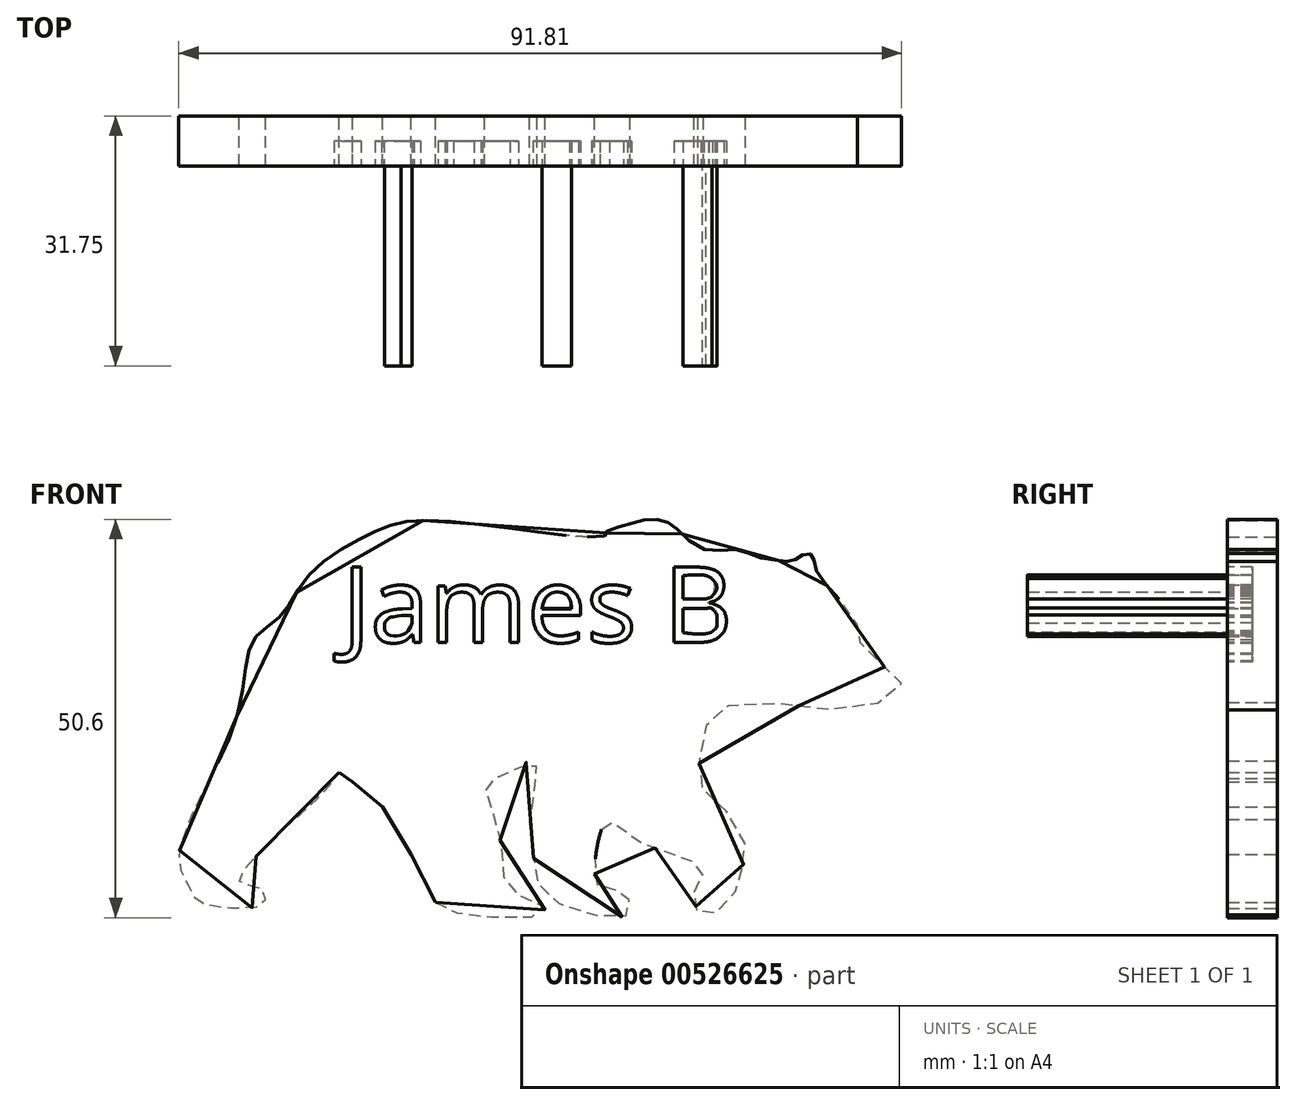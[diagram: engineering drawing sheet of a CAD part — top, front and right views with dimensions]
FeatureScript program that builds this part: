
annotation { "Feature Type Name" : "Feature", "Feature Type Description" : "" }
export const myFeature = defineFeature(function(context is Context, id is Id, definition is map)
    precondition{}
    {
        {
            var Q0;
            Q0=qCreatedBy(makeId("Front.planeOp"),FACE);
            var sketch = newSketch(context, id + "F0", { "sketchPlane" : qUnion([Q0])});
            skLineSegment(sketch, "E0", {"start": v(-22.8, 11.9) * mm, "end": v(-21.08, 10.75) * mm});
            skLineSegment(sketch, "E1", {"start": v(-21.08, 10.75) * mm, "end": v(-17.32, 7.58) * mm});
            skLineSegment(sketch, "E2", {"start": v(-17.32, 7.58) * mm, "end": v(-13.67, 1.51) * mm});
            skLineSegment(sketch, "E3", {"start": v(-13.67, 1.51) * mm, "end": v(-10.59, -4.55) * mm});
            skPoint(sketch, "E4.69.internal.snap0", {"position": v(-19.2, 9.16) * mm});
            skPoint(sketch, "E4.87.internal.snap0", {"position": v(-19.2, 9.16) * mm});
            skFitSpline(sketch, "E4", {"points": [v(-10.59, -4.55) * mm, v(-8.16, -5.82) * mm, v(-2.34, -6.46) * mm, v(3.16, -5.98) * mm, v(3.03, -5.02) * mm, v(0, -3.69) * mm, v(-1.74, -1.92) * mm, v(-2.18, 2.8) * mm, v(-2.28, 2.98) * mm, v(-3.2, 6.92) * mm, v(-4.2, 11.04) * mm, v(-1.6, 11.32) * mm, v(1.25, 13.36) * mm, v(2.2, 12.81) * mm, v(2.07, 10.36) * mm, v(1.39, 4.78) * mm, v(2.07, 0) * mm, v(2.75, -2.84) * mm, v(7.51, -5.7) * mm, v(13.23, -6.37) * mm, v(14.11, -5.73) * mm, v(13.97, -4.1) * mm, v(13.4, -3.38) * mm, v(11.15, -2.8) * mm, v(9.93, -2.22) * mm, v(9.79, 1.35) * mm, v(10.97, 5.58) * mm, v(11.64, 5.91) * mm, v(12.84, 4.47) * mm, v(22.37, 0.52) * mm, v(23.48, -0.44) * mm, v(22.85, -1.98) * mm, v(22.27, -3.23) * mm, v(22.47, -4.55) * mm, v(22.75, -5.92) * mm, v(24.77, -5.97) * mm, v(27.32, -3.76) * mm, v(28.2, -0.73) * mm, v(28.48, 0) * mm, v(28.53, 3.99) * mm, v(24.78, 8.4) * mm, v(22.83, 11.14) * mm, v(23.64, 16.4) * mm, v(24.8, 19.65) * mm, v(32.7, 20.74) * mm, v(43.85, 20.2) * mm, v(48.61, 23.05) * mm, v(47.8, 24.16) * mm, v(44.32, 27.4) * mm, v(42.95, 29.26) * mm, v(43.03, 30.72) * mm, v(40.3, 34.4) * mm, v(37.64, 37.96) * mm, v(37.37, 39.46) * mm, v(36.7, 39.73) * mm, v(35.67, 39.39) * mm, v(34.85, 38.84) * mm, v(33.09, 38.84) * mm, v(30.1, 39.39) * mm, v(27.5, 40.27) * mm, v(23.7, 40.2) * mm, v(20.02, 42.93) * mm, v(18.48, 43.89) * mm, v(16.03, 44.03) * mm, v(13.82, 43.4) * mm, v(11.27, 42.59) * mm, v(11.12, 42.1) * mm, v(2.22, 42.5) * mm, v(-13.4, 43.92) * mm, v(-19.2, 42.08) * mm, v(-26.5, 37.18) * mm, v(-30.23, 31.84) * mm, v(-33.79, 28.6) * mm, v(-35.57, 19.87) * mm, v(-40.99, 7.7) * mm, v(-42.36, 4.38) * mm, v(-43.06, 2.2) * mm, v(-42.92, -0.52) * mm, v(-41.43, -3.44) * mm, v(-40.61, -4.55) * mm, v(-33, -5.07) * mm, v(-32.17, -3.92) * mm, v(-33, -2.62) * mm, v(-35.1, -2.28) * mm, v(-35.44, -1.33) * mm, v(-32.51, 2.07) * mm, v(-29.11, 5.4) * mm, v(-25.03, 9.16) * mm, v(-22.8, 11.9) * mm], "startDerivative": vector(206.86, -137.7) * mm, "endDerivative": vector(164.22, 225.3) * mm});
            skSolve(sketch);
        }
        {
            var Q0;
            Q0 = qSketchRegion(id + "F0", true);
            extrude(context, id + "F1", {"entities" : qUnion([Q0]), "depth" : 6.35 * mm, "offsetDistance" : 25.4 * mm});
        }
        {
            var Q0;
            Q0=makeQuery(id+"F1.opExtrude","CAP_FACE",FACE,{"disambiguationData":[OSD([sQuery(id+"F0.wireOp",EDGE,"E0"),sQuery(id+"F0.wireOp",EDGE,"E1"),sQuery(id+"F0.wireOp",EDGE,"E2"),sQuery(id+"F0.wireOp",EDGE,"E3"),sQuery(id+"F0.wireOp",EDGE,"E4")])],"isStart":false});
            var sketch = newSketch(context, id + "F2", { "sketchPlane" : qUnion([Q0])});
            skText(sketch, "E5", { "text": "James B", "fontName": "OpenSans-Regular.ttf"});
            const initialGuessF2  = {"E5": [-0.02241, 0.02846, 1, 0, 0.00964]};
            skSetInitialGuess(sketch, initialGuessF2);
            skSolve(sketch);
        }
        {
            var Q0;
            Q0=makeQuery(id+"F2.imprint","IMPRINT",FACE,{"disambiguationData":[TD([[makeQuery(id+"F2.imprint","IMPRINT",EDGE,{"derivedFrom":sQuery(id+"F2.wireOp",EDGE,"E5.sketch_text.stroke-0")}),1.0]])]});
            var sketch = newSketch(context, id + "F3", { "sketchPlane" : qUnion([Q0])});
            skLineSegment(sketch, "E6", {"start": v(-21.16, 38.02) * mm, "end": v(-21.16, 28.58) * mm});
            skLineSegment(sketch, "E7", {"start": v(-21.16, 38.02) * mm, "end": v(-19.95, 38.02) * mm});
            skLineSegment(sketch, "E8", {"start": v(-19.95, 38.02) * mm, "end": v(-19.95, 28.64) * mm});
            skFitSpline(sketch, "E9", {"points": [v(-21.16, 28.58) * mm, v(-21.16, 27.92) * mm, v(-21.82, 27.2) * mm, v(-23.27, 27) * mm, v(-23.4, 26.16) * mm, v(-22.6, 26.04) * mm, v(-21.7, 26.1) * mm, v(-20.73, 26.59) * mm, v(-19.95, 27.67) * mm], "startDerivative": vector(0.93, -6.27) * mm, "endDerivative": vector(4.85, 8.31) * mm});
            skLineSegment(sketch, "E10", {"start": v(-19.95, 28.64) * mm, "end": v(-19.95, 27.67) * mm});
            skLineSegment(sketch, "E11", {"start": v(-17.3, 35.15) * mm, "end": v(-17, 34.47) * mm});
            skLineSegment(sketch, "E12", {"start": v(-13.47, 29.43) * mm, "end": v(-13.22, 28.52) * mm});
            skLineSegment(sketch, "E13", {"start": v(-13.56, 31.9) * mm, "end": v(-13.56, 30.9) * mm});
            skLineSegment(sketch, "E14", {"start": v(-13.22, 28.52) * mm, "end": v(-12.53, 28.52) * mm});
            skLineSegment(sketch, "E15", {"start": v(-12.53, 28.52) * mm, "end": v(-12.53, 33.42) * mm});
            skLineSegment(sketch, "E16", {"start": v(-13.56, 32.84) * mm, "end": v(-13.56, 33.48) * mm});
            skFitSpline(sketch, "E17", {"points": [v(-17.3, 35.15) * mm, v(-16.1, 35.63) * mm, v(-14.92, 35.72) * mm, v(-14.04, 35.63) * mm, v(-13.13, 35.15) * mm, v(-12.53, 34.24) * mm, v(-12.53, 33.42) * mm], "startDerivative": vector(6.35, 3.06) * mm, "endDerivative": vector(-0.75, -5.45) * mm});
            skFitSpline(sketch, "E18", {"points": [v(-17, 34.47) * mm, v(-16.18, 34.78) * mm, v(-15.27, 34.96) * mm, v(-14.46, 34.9) * mm, v(-13.7, 34.47) * mm, v(-13.56, 33.48) * mm], "startDerivative": vector(4.02, 1.7) * mm, "endDerivative": vector(-0.15, -5.26) * mm});
            skFitSpline(sketch, "E19", {"points": [v(-13.56, 32.84) * mm, v(-14.6, 32.84) * mm, v(-16.42, 32.57) * mm, v(-17.88, 31.82) * mm, v(-18.27, 30.27) * mm, v(-17.97, 29.33) * mm, v(-17.33, 28.64) * mm, v(-16.21, 28.34) * mm, v(-14.43, 28.55) * mm, v(-13.47, 29.43) * mm], "startDerivative": vector(-9.94, 0.36) * mm, "endDerivative": vector(7.38, 9.37) * mm});
            skFitSpline(sketch, "E20", {"points": [v(-13.56, 31.9) * mm, v(-14.97, 31.9) * mm], "startDerivative": vector(-1.42, 0) * mm, "endDerivative": vector(-1.42, 0) * mm});
            skFitSpline(sketch, "E21", {"points": [v(-14.97, 31.9) * mm, v(-15.85, 31.72) * mm, v(-16.33, 31.63) * mm, v(-17, 30.97) * mm, v(-17.03, 30.33) * mm, v(-16.88, 29.73) * mm, v(-16.21, 29.3) * mm, v(-14.97, 29.33) * mm, v(-14, 29.94) * mm, v(-13.56, 30.9) * mm], "startDerivative": vector(-8.4, -2.05) * mm, "endDerivative": vector(2.73, 8.36) * mm});
            skLineSegment(sketch, "E22", {"start": v(-10.25, 35.6) * mm, "end": v(-10.25, 28.58) * mm});
            skLineSegment(sketch, "E23", {"start": v(-5.65, 33.33) * mm, "end": v(-5.65, 28.62) * mm});
            skLineSegment(sketch, "E24", {"start": v(-4.49, 33.35) * mm, "end": v(-4.49, 28.57) * mm});
            skLineSegment(sketch, "E25", {"start": v(-9.07, 33.2) * mm, "end": v(-9.07, 28.62) * mm});
            skLineSegment(sketch, "E26", {"start": v(-9.3, 35.6) * mm, "end": v(-9.3, 34.79) * mm});
            skLineSegment(sketch, "E27", {"start": v(-5.65, 28.62) * mm, "end": v(-4.49, 28.57) * mm});
            skLineSegment(sketch, "E28", {"start": v(0, 33.46) * mm, "end": v(0, 28.59) * mm});
            skLineSegment(sketch, "E29", {"start": v(0, 28.59) * mm, "end": v(-1.09, 28.59) * mm});
            skLineSegment(sketch, "E30", {"start": v(-1.09, 28.59) * mm, "end": v(-1.09, 33.42) * mm});
            skFitSpline(sketch, "E31", {"points": [v(-9.07, 33.2) * mm, v(-8.7, 34.2) * mm, v(-7.98, 34.66) * mm, v(-6.95, 34.88) * mm, v(-6.05, 34.58) * mm, v(-5.65, 33.33) * mm], "startDerivative": vector(1.27, 5.5) * mm, "endDerivative": vector(1, -6.51) * mm});
            skLineSegment(sketch, "E32", {"start": v(-10.25, 35.6) * mm, "end": v(-9.3, 35.6) * mm});
            skFitSpline(sketch, "E33", {"points": [v(-4.49, 33.35) * mm, v(-4.3, 33.98) * mm, v(-4.06, 34.28) * mm, v(-3.83, 34.52) * mm, v(-3.44, 34.72) * mm, v(-3.05, 34.8) * mm, v(-2.75, 34.83) * mm, v(-2.5, 34.83) * mm, v(-2.16, 34.8) * mm, v(-1.79, 34.67) * mm, v(-1.42, 34.37) * mm], "startDerivative": vector(1.09, 5.4) * mm, "endDerivative": vector(3.24, -3.12) * mm});
            skFitSpline(sketch, "E34", {"points": [v(-1.09, 33.42) * mm, v(-1.17, 33.77) * mm, v(-1.27, 34.1) * mm, v(-1.42, 34.37) * mm], "startDerivative": vector(-0.21, 1.02) * mm, "endDerivative": vector(-0.49, 0.8) * mm});
            skLineSegment(sketch, "E35", {"start": v(-10.25, 28.58) * mm, "end": v(-9.07, 28.62) * mm});
            skFitSpline(sketch, "E36", {"points": [v(0, 33.46) * mm, v(-0.15, 34.31) * mm, v(-0.6, 35.11) * mm, v(-1.35, 35.6) * mm, v(-2.01, 35.74) * mm, v(-2.88, 35.74) * mm, v(-3.5, 35.58) * mm, v(-4.24, 35.17) * mm, v(-4.68, 34.66) * mm, v(-4.74, 34.56) * mm, v(-4.8, 34.55) * mm, v(-4.95, 34.85) * mm], "startDerivative": vector(-0.88, 7.61) * mm, "endDerivative": vector(-2.24, 5.77) * mm});
            skFitSpline(sketch, "E37", {"points": [v(-4.95, 34.85) * mm, v(-5.33, 35.26) * mm, v(-6.08, 35.65) * mm], "startDerivative": vector(-0.71, 0.97) * mm, "endDerivative": vector(-1.5, 0.66) * mm});
            skFitSpline(sketch, "E38", {"points": [v(-6.08, 35.65) * mm, v(-6.75, 35.78) * mm, v(-7.65, 35.7) * mm, v(-8.64, 35.25) * mm, v(-9.01, 34.85) * mm, v(-9.1, 34.63) * mm, v(-9.17, 34.62) * mm, v(-9.3, 34.79) * mm], "startDerivative": vector(-3.77, 0.94) * mm, "endDerivative": vector(-1.28, 2.28) * mm});
            skLineSegment(sketch, "E39", {"start": v(2.95, 32.74) * mm, "end": v(6.67, 32.74) * mm});
            skLineSegment(sketch, "E40", {"start": v(2.95, 31.84) * mm, "end": v(7.85, 31.84) * mm});
            skFitSpline(sketch, "E41", {"points": [v(6.67, 32.74) * mm, v(6.67, 33.3) * mm, v(6.4, 34.1) * mm, v(5.8, 34.66) * mm, v(4.87, 34.86) * mm, v(4.16, 34.69) * mm, v(3.56, 34.24) * mm, v(3.2, 33.62) * mm, v(2.95, 32.74) * mm], "startDerivative": vector(0.34, 4.94) * mm, "endDerivative": vector(-1.67, -6.77) * mm});
            skLineSegment(sketch, "E42", {"start": v(7.58, 29.74) * mm, "end": v(7.58, 28.8) * mm});
            skFitSpline(sketch, "E43", {"points": [v(7.58, 29.74) * mm, v(6.98, 29.55) * mm, v(5.79, 29.27) * mm, v(4.23, 29.44) * mm, v(3.35, 30.2) * mm, v(2.95, 31.84) * mm], "startDerivative": vector(-3.85, -1.25) * mm, "endDerivative": vector(-1.07, 7.7) * mm});
            skFitSpline(sketch, "E44", {"points": [v(7.58, 28.8) * mm, v(6.56, 28.44) * mm, v(4.78, 28.35) * mm, v(3.26, 28.8) * mm, v(2.26, 29.96) * mm, v(1.85, 31.24) * mm, v(1.92, 32.93) * mm, v(2.5, 34.56) * mm], "startDerivative": vector(-7.76, -3.44) * mm, "endDerivative": vector(4.52, 10.44) * mm});
            skFitSpline(sketch, "E45", {"points": [v(2.5, 34.56) * mm, v(3.06, 35.15) * mm, v(4.16, 35.67) * mm], "startDerivative": vector(1.09, 1.4) * mm, "endDerivative": vector(2.21, 0.83) * mm});
            skFitSpline(sketch, "E46", {"points": [v(4.16, 35.67) * mm, v(4.8, 35.74) * mm], "startDerivative": vector(0.63, 0.07) * mm, "endDerivative": vector(0.63, 0.07) * mm});
            skFitSpline(sketch, "E47", {"points": [v(4.8, 35.74) * mm, v(5.37, 35.74) * mm, v(6.2, 35.48) * mm, v(6.89, 35.16) * mm, v(7.25, 34.69) * mm, v(7.58, 34.13) * mm, v(7.8, 33.53) * mm, v(7.87, 32.98) * mm, v(7.85, 31.84) * mm], "startDerivative": vector(4.9, 0.44) * mm, "endDerivative": vector(-0.3, -7.92) * mm});
            skFitSpline(sketch, "E48", {"points": [v(9.35, 29.74) * mm, v(10.63, 29.35) * mm], "startDerivative": vector(1.28, -0.39) * mm, "endDerivative": vector(1.28, -0.39) * mm});
            skFitSpline(sketch, "E49", {"points": [v(10.63, 29.35) * mm, v(11.48, 29.35) * mm, v(12.38, 29.35) * mm], "startDerivative": vector(1.72, 0) * mm, "endDerivative": vector(1.79, 0) * mm});
            skFitSpline(sketch, "E50", {"points": [v(12.38, 29.35) * mm, v(12.73, 29.48) * mm, v(13.37, 30.12) * mm, v(13.15, 30.93) * mm, v(11.31, 31.88) * mm, v(9.52, 32.82) * mm, v(9.22, 33.84) * mm, v(9.52, 34.83) * mm], "startDerivative": vector(3.72, 0.95) * mm, "endDerivative": vector(2.92, 6.98) * mm});
            skFitSpline(sketch, "E51", {"points": [v(13.75, 34.44) * mm, v(11.91, 34.87) * mm, v(10.63, 34.53) * mm], "startDerivative": vector(-3.54, 1.2) * mm, "endDerivative": vector(-2.68, -1.1) * mm});
            skFitSpline(sketch, "E52", {"points": [v(10.63, 34.53) * mm, v(10.2, 33.97) * mm, v(10.63, 33.33) * mm, v(11.7, 32.77) * mm, v(12.98, 32.26) * mm], "startDerivative": vector(-2.96, -2.53) * mm, "endDerivative": vector(4.4, -1.74) * mm});
            skFitSpline(sketch, "E53", {"points": [v(12.98, 32.26) * mm, v(14, 31.5) * mm], "startDerivative": vector(1.03, -0.77) * mm, "endDerivative": vector(1.03, -0.77) * mm});
            skFitSpline(sketch, "E54", {"points": [v(14, 31.5) * mm, v(14.3, 30.93) * mm, v(14.35, 30.2) * mm, v(14.1, 29.27) * mm, v(12.98, 28.5) * mm, v(11.23, 28.28) * mm, v(9.56, 28.62) * mm, v(9.35, 29.74) * mm], "startDerivative": vector(3.38, -5.02) * mm, "endDerivative": vector(0.4, 9.11) * mm});
            skFitSpline(sketch, "E55", {"points": [v(9.52, 34.83) * mm, v(10.2, 35.47) * mm, v(11.7, 35.77) * mm], "startDerivative": vector(1.31, 1.66) * mm, "endDerivative": vector(2.98, 0.27) * mm});
            skFitSpline(sketch, "E56", {"points": [v(13.75, 34.44) * mm, v(14.3, 35.26) * mm, v(11.7, 35.77) * mm], "startDerivative": vector(2.54, 2.4) * mm, "endDerivative": vector(-5.96, 0.41) * mm});
            skLineSegment(sketch, "E57", {"start": v(19.74, 38.04) * mm, "end": v(19.74, 28.54) * mm});
            skLineSegment(sketch, "E58", {"start": v(20.9, 36.95) * mm, "end": v(20.9, 33.99) * mm});
            skLineSegment(sketch, "E59", {"start": v(20.9, 32.78) * mm, "end": v(20.9, 29.69) * mm});
            skLineSegment(sketch, "E60", {"start": v(19.74, 38.04) * mm, "end": v(23.01, 38.04) * mm});
            skLineSegment(sketch, "E61", {"start": v(20.9, 32.78) * mm, "end": v(23.25, 32.78) * mm});
            skFitSpline(sketch, "E62", {"points": [v(19.74, 28.54) * mm, v(22.16, 28.54) * mm, v(23.98, 28.54) * mm, v(25.86, 29.45) * mm, v(26.46, 30.96) * mm, v(26.16, 32.53) * mm, v(24.52, 33.44) * mm], "startDerivative": vector(13.43, 0.3) * mm, "endDerivative": vector(-11.75, 4.18) * mm});
            skFitSpline(sketch, "E63", {"points": [v(24.52, 33.44) * mm, v(25.67, 34.29) * mm, v(26.1, 35.62) * mm, v(25.5, 37.2) * mm, v(23.01, 38.04) * mm], "startDerivative": vector(5.74, 3.25) * mm, "endDerivative": vector(-9.49, 1.7) * mm});
            skFitSpline(sketch, "E64", {"points": [v(20.9, 33.99) * mm, v(23.8, 33.99) * mm], "startDerivative": vector(2.9, 0) * mm, "endDerivative": vector(2.9, 0) * mm});
            skFitSpline(sketch, "E65", {"points": [v(23.8, 33.99) * mm, v(24.52, 34.29) * mm, v(25.17, 35.44) * mm, v(24.52, 36.59) * mm], "startDerivative": vector(2.59, 0.6) * mm, "endDerivative": vector(-2.7, 3.03) * mm});
            skFitSpline(sketch, "E66", {"points": [v(20.9, 36.95) * mm, v(23.8, 36.95) * mm, v(24.52, 36.59) * mm], "startDerivative": vector(5.2, 0.34) * mm, "endDerivative": vector(1.7, -1.23) * mm});
            skFitSpline(sketch, "E67", {"points": [v(23.25, 32.78) * mm, v(23.8, 32.78) * mm, v(24.52, 32.78) * mm, v(25.17, 31.93) * mm], "startDerivative": vector(1.83, -0.12) * mm, "endDerivative": vector(1.45, -2.78) * mm});
            skFitSpline(sketch, "E68", {"points": [v(25.17, 31.93) * mm, v(25.17, 30.96) * mm, v(25.17, 30.48) * mm, v(24.52, 29.81) * mm, v(23.25, 29.5) * mm, v(20.9, 29.69) * mm], "startDerivative": vector(-0.22, -5.74) * mm, "endDerivative": vector(-8.74, 1.04) * mm});
            skSolve(sketch);
        }
        {
            var Q0;
            Q0=makeQuery(id+"F3.imprint","IMPRINT",FACE,{"disambiguationData":[TD([[makeQuery(id+"F3.imprint","IMPRINT",EDGE,{"derivedFrom":sQuery(id+"F3.wireOp",EDGE,"E58")}),-1.0]])]});
            var Q1;
            Q1 = qSketchRegion(id + "F2", true);
            var Q2;
            Q2=makeQuery(id+"F2.imprint","IMPRINT",FACE,{"disambiguationData":[TD([[makeQuery(id+"F2.imprint","IMPRINT",EDGE,{"derivedFrom":sQuery(id+"F2.wireOp",EDGE,"E5.sketch_text.stroke-29")}),1.0]])]});
            extrude(context, id + "F4", {"entities" : qUnion([Q0, Q1, Q2]), "operationType" : NewBodyOperationType.REMOVE, "oppositeDirection" : true, "depth" : 3.17 * mm, "offsetDistance" : 25.4 * mm});
        }
        {
            var Q0;
            Q0=makeQuery(id+"F3.imprint","IMPRINT",FACE,{"disambiguationData":[TD([[makeQuery(id+"F3.imprint","IMPRINT",EDGE,{"derivedFrom":sQuery(id+"F3.wireOp",EDGE,"E13")}),-1.0]])]});
            var Q1;
            Q1=makeQuery(id+"F3.imprint","IMPRINT",FACE,{"disambiguationData":[TD([[makeQuery(id+"F3.imprint","IMPRINT",EDGE,{"derivedFrom":sQuery(id+"F3.wireOp",EDGE,"E39")}),1.0]])]});
            var Q2;
            Q2=makeQuery(id+"F3.imprint","IMPRINT",FACE,{"disambiguationData":[TD([[makeQuery(id+"F3.imprint","IMPRINT",EDGE,{"derivedFrom":sQuery(id+"F3.wireOp",EDGE,"E58")}),1.0]])]});
            var Q3;
            Q3=makeQuery(id+"F3.imprint","IMPRINT",FACE,{"disambiguationData":[TD([[makeQuery(id+"F3.imprint","IMPRINT",EDGE,{"derivedFrom":sQuery(id+"F3.wireOp",EDGE,"E59")}),1.0]])]});
            extrude(context, id + "F5", {"entities" : qUnion([Q0, Q1, Q2, Q3]), "operationType" : NewBodyOperationType.ADD, "depth" : 25.4 * mm, "offsetDistance" : 25.4 * mm});
        }
    });
